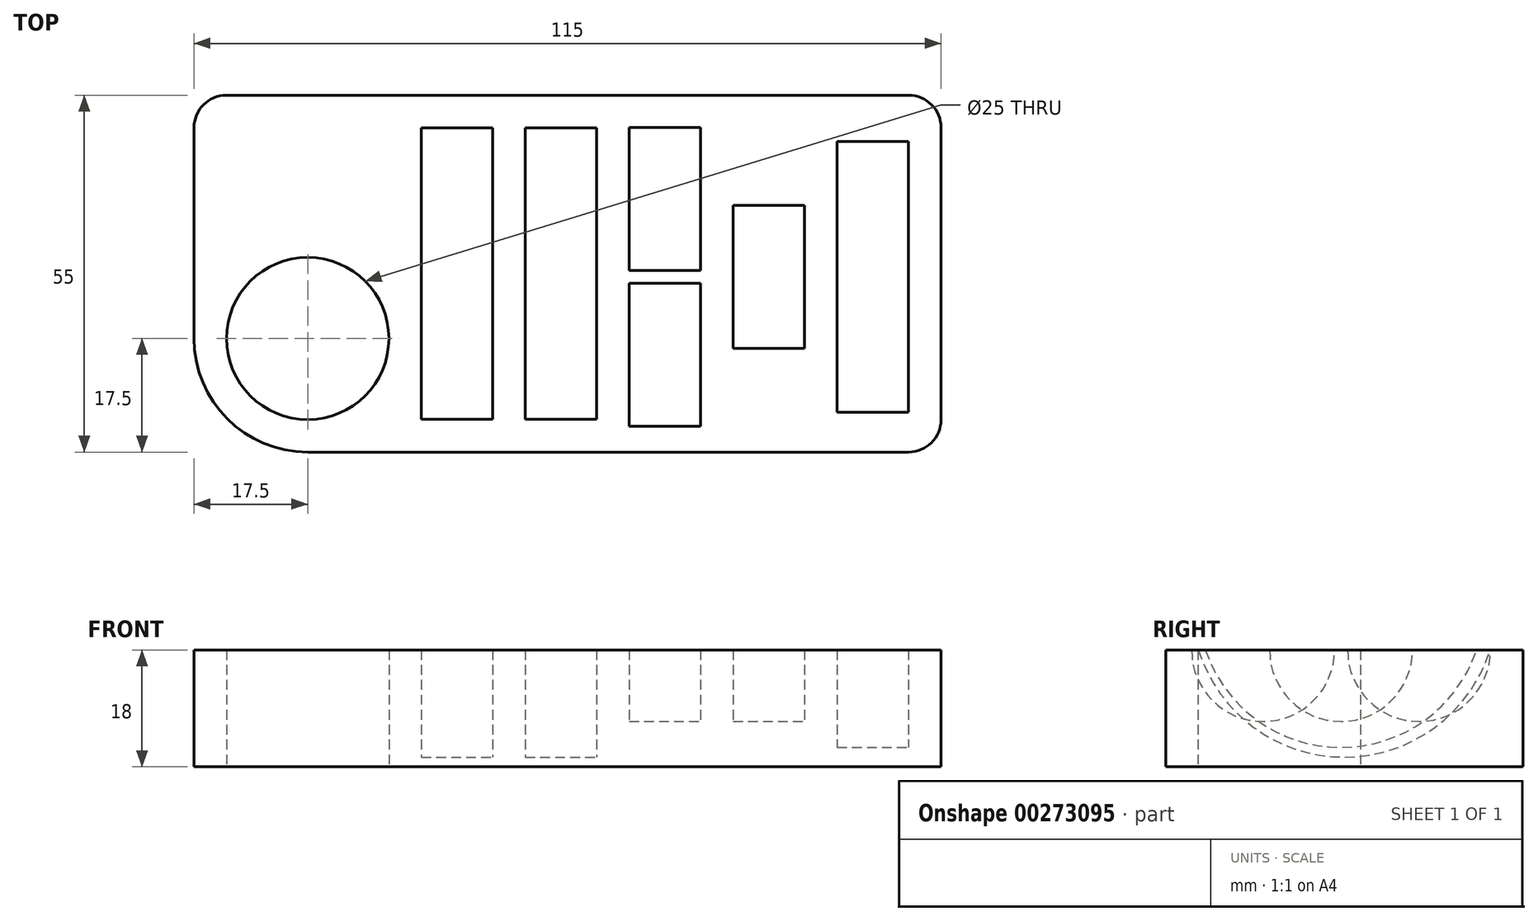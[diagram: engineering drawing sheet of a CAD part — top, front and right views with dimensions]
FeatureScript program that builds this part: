
annotation { "Feature Type Name" : "Feature", "Feature Type Description" : "" }
export const myFeature = defineFeature(function(context is Context, id is Id, definition is map)
    precondition{}
    {
        {
            var Q0;
            Q0=qCreatedBy(makeId("Top.planeOp"),FACE);
            var sketch = newSketch(context, id + "F0", { "sketchPlane" : qUnion([Q0])});
            skLineSegment(sketch, "E0.bottom", {"start": v(17.5, 0) * mm, "end": v(110, 0) * mm});
            skLineSegment(sketch, "E0.top", {"start": v(5, 55) * mm, "end": v(110, 55) * mm});
            skLineSegment(sketch, "E0.left", {"start": v(0, 17.5) * mm, "end": v(0, 50) * mm});
            skLineSegment(sketch, "E0.right", {"start": v(115, 5) * mm, "end": v(115, 50) * mm});
            skLineSegment(sketch, "E1.bottom", {"start": v(0, 0) * mm, "end": v(17.5, 0) * mm, "construction": true});
            skLineSegment(sketch, "E1.top", {"start": v(0, 17.5) * mm, "end": v(17.5, 17.5) * mm, "construction": true});
            skLineSegment(sketch, "E1.left", {"start": v(0, 0) * mm, "end": v(0, 17.5) * mm, "construction": true});
            skLineSegment(sketch, "E1.right", {"start": v(17.5, 0) * mm, "end": v(17.5, 17.5) * mm, "construction": true});
            skCircle(sketch, "E2", {"center": v(17.5, 17.5) * mm, "radius": 12.5 * mm});
            skPoint(sketch, "E3.visualSharp", {"position": v(0, 0) * mm});
            skArc(sketch, "E3.filletArc", {"start": v(0, 17.5) * mm, "mid": v(5.13, 5.13) * mm, "end": v(17.5, 0) * mm});
            skPoint(sketch, "E4.visualSharp", {"position": v(0, 55) * mm});
            skArc(sketch, "E4.filletArc", {"start": v(5, 55) * mm, "mid": v(1.46, 53.54) * mm, "end": v(0, 50) * mm});
            skPoint(sketch, "E5.visualSharp", {"position": v(115, 55) * mm});
            skArc(sketch, "E5.filletArc", {"start": v(115, 50) * mm, "mid": v(113.54, 53.54) * mm, "end": v(110, 55) * mm});
            skPoint(sketch, "E6.visualSharp", {"position": v(115, 0) * mm});
            skArc(sketch, "E6.filletArc", {"start": v(110, 0) * mm, "mid": v(113.54, 1.46) * mm, "end": v(115, 5) * mm});
            skSolve(sketch);
        }
        {
            var Q0;
            Q0=makeQuery(id+"F0.imprint","IMPRINT",FACE,{"disambiguationData":[TD([[makeQuery(id+"F0.imprint","IMPRINT",EDGE,{"derivedFrom":sQuery(id+"F0.wireOp",EDGE,"E0.bottom")}),1.0]])]});
            extrude(context, id + "F1", {"entities" : qUnion([Q0]), "depth" : 25 * mm});
        }
        {
            var Q0;
            Q0=makeQuery(id+"F1.opExtrude","CAP_FACE",FACE,{"disambiguationData":[OSD([sQuery(id+"F0.wireOp",EDGE,"E0.bottom"),sQuery(id+"F0.wireOp",EDGE,"E0.top"),sQuery(id+"F0.wireOp",EDGE,"E0.right"),sQuery(id+"F0.wireOp",EDGE,"E2"),sQuery(id+"F0.wireOp",EDGE,"E3.filletArc"),sQuery(id+"F0.wireOp",EDGE,"E4.filletArc"),sQuery(id+"F0.wireOp",EDGE,"E5.filletArc"),sQuery(id+"F0.wireOp",EDGE,"E6.filletArc")])],"isStart":false});
            var sketch = newSketch(context, id + "F2", { "sketchPlane" : qUnion([Q0])});
            skLineSegment(sketch, "E7.bottom", {"start": v(0, 0) * mm, "end": v(35, 0) * mm, "construction": true});
            skLineSegment(sketch, "E7.top", {"start": v(0, 27.5) * mm, "end": v(35, 27.5) * mm, "construction": true});
            skLineSegment(sketch, "E7.left", {"start": v(0, 0) * mm, "end": v(0, 27.5) * mm, "construction": true});
            skLineSegment(sketch, "E7.right", {"start": v(35, 0) * mm, "end": v(35, 27.5) * mm, "construction": true});
            skLineSegment(sketch, "E8.bottom", {"start": v(35, 27.5) * mm, "end": v(46, 27.5) * mm});
            skLineSegment(sketch, "E8.top", {"start": v(35, 4) * mm, "end": v(46, 4) * mm});
            skLineSegment(sketch, "E8.left", {"start": v(35, 27.5) * mm, "end": v(35, 4) * mm});
            skLineSegment(sketch, "E8.right", {"start": v(46, 27.5) * mm, "end": v(46, 4) * mm});
            skLineSegment(sketch, "E9", {"start": v(46, 27.5) * mm, "end": v(51, 27.5) * mm, "construction": true});
            skLineSegment(sketch, "E10.bottom", {"start": v(51, 27.5) * mm, "end": v(62, 27.5) * mm});
            skLineSegment(sketch, "E10.top", {"start": v(51, 4) * mm, "end": v(62, 4) * mm});
            skLineSegment(sketch, "E10.left", {"start": v(51, 27.5) * mm, "end": v(51, 4) * mm});
            skLineSegment(sketch, "E10.right", {"start": v(62, 27.5) * mm, "end": v(62, 4) * mm});
            skSolve(sketch);
        }
        {
            var Q0;
            Q0=makeQuery(id+"F2.imprint","IMPRINT",FACE,{"disambiguationData":[TD([[makeQuery(id+"F2.imprint","IMPRINT",EDGE,{"derivedFrom":sQuery(id+"F2.wireOp",EDGE,"E8.bottom")}),-1.0]])]});
            var Q1;
            Q1=makeQuery(id+"F2.imprint","IMPRINT",FACE,{"disambiguationData":[TD([[makeQuery(id+"F2.imprint","IMPRINT",EDGE,{"derivedFrom":sQuery(id+"F2.wireOp",EDGE,"E10.bottom")}),-1.0]])]});
            var Q2;
            Q2=sQuery(id+"F2.wireOp",EDGE,"E8.bottom");
            revolve(context, id + "F3", {"operationType" : NewBodyOperationType.REMOVE, "entities" : qUnion([Q0, Q1]), "axis" : qUnion([Q2]), "revolveType" : RevolveType.FULL, "oppositeDirection" : true});
        }
        {
            var Q0;
            Q0=makeQuery(id+"F1.opExtrude","SWEPT_FACE",FACE,{"disambiguationData":[OSD([sQuery(id+"F0.wireOp",EDGE,"E0.bottom")])]});
            var sketch = newSketch(context, id + "F4", { "sketchPlane" : qUnion([Q0])});
            skLineSegment(sketch, "E11", {"start": v(0, 0) * mm, "end": v(0, 18) * mm, "construction": true});
            skLineSegment(sketch, "E12.bottom", {"start": v(0, 18) * mm, "end": v(147.38, 18) * mm});
            skLineSegment(sketch, "E12.top", {"start": v(0, 40) * mm, "end": v(147.38, 40) * mm});
            skLineSegment(sketch, "E12.left", {"start": v(0, 18) * mm, "end": v(0, 40) * mm});
            skLineSegment(sketch, "E12.right", {"start": v(147.38, 18) * mm, "end": v(147.38, 40) * mm});
            skSolve(sketch);
        }
        {
            var Q0;
            Q0=qSketchRegion(id+"F4",true);
            extrude(context, id + "F5", {"entities" : qUnion([Q0]), "operationType" : NewBodyOperationType.REMOVE, "endBound" : BoundingType.THROUGH_ALL, "oppositeDirection" : true, "depth" : 25 * mm});
        }
        {
            var Q0;
            Q0=makeQuery(id+"F5.boolean.opBoolean","COPY",FACE,{"derivedFrom":makeQuery(id+"F5.opExtrude","SWEPT_FACE",FACE,{"disambiguationData":[OSD([sQuery(id+"F4.wireOp",EDGE,"E12.bottom")])]})});
            var sketch = newSketch(context, id + "F6", { "sketchPlane" : qUnion([Q0])});
            skLineSegment(sketch, "E13.bottom", {"start": v(0, 0) * mm, "end": v(67, 0) * mm, "construction": true});
            skLineSegment(sketch, "E13.top", {"start": v(0, 4) * mm, "end": v(67, 4) * mm, "construction": true});
            skLineSegment(sketch, "E13.left", {"start": v(0, 0) * mm, "end": v(0, 4) * mm, "construction": true});
            skLineSegment(sketch, "E13.right", {"start": v(67, 0) * mm, "end": v(67, 4) * mm, "construction": true});
            skLineSegment(sketch, "E14", {"start": v(67, 4) * mm, "end": v(67, 50) * mm, "construction": true});
            skLineSegment(sketch, "E15.bottom", {"start": v(67, 4) * mm, "end": v(78, 4) * mm});
            skLineSegment(sketch, "E15.top", {"start": v(67, 15) * mm, "end": v(78, 15) * mm});
            skLineSegment(sketch, "E15.left", {"start": v(67, 4) * mm, "end": v(67, 15) * mm});
            skLineSegment(sketch, "E15.right", {"start": v(78, 4) * mm, "end": v(78, 15) * mm});
            skLineSegment(sketch, "E16.bottom", {"start": v(67, 50) * mm, "end": v(78, 50) * mm});
            skLineSegment(sketch, "E16.top", {"start": v(67, 39) * mm, "end": v(78, 39) * mm});
            skLineSegment(sketch, "E16.left", {"start": v(67, 50) * mm, "end": v(67, 39) * mm});
            skLineSegment(sketch, "E16.right", {"start": v(78, 50) * mm, "end": v(78, 39) * mm});
            skLineSegment(sketch, "E17", {"start": v(67, 27) * mm, "end": v(83, 27) * mm, "construction": true});
            skLineSegment(sketch, "E18.bottom", {"start": v(83, 27) * mm, "end": v(94, 27) * mm});
            skLineSegment(sketch, "E18.top", {"start": v(83, 16) * mm, "end": v(94, 16) * mm});
            skLineSegment(sketch, "E18.left", {"start": v(83, 27) * mm, "end": v(83, 16) * mm});
            skLineSegment(sketch, "E18.right", {"start": v(94, 27) * mm, "end": v(94, 16) * mm});
            skSolve(sketch);
        }
        {
            var Q0;
            Q0=makeQuery(id+"F6.imprint","IMPRINT",FACE,{"disambiguationData":[TD([[makeQuery(id+"F6.imprint","IMPRINT",EDGE,{"derivedFrom":sQuery(id+"F6.wireOp",EDGE,"E15.bottom")}),1.0]])]});
            var Q1;
            Q1=sQuery(id+"F6.wireOp",EDGE,"E15.top");
            revolve(context, id + "F7", {"operationType" : NewBodyOperationType.REMOVE, "entities" : qUnion([Q0]), "axis" : qUnion([Q1]), "revolveType" : RevolveType.FULL, "oppositeDirection" : true});
        }
        {
            var Q0;
            Q0=makeQuery(id+"F6.imprint","IMPRINT",FACE,{"disambiguationData":[TD([[makeQuery(id+"F6.imprint","IMPRINT",EDGE,{"derivedFrom":sQuery(id+"F6.wireOp",EDGE,"E18.bottom")}),-1.0]])]});
            var Q1;
            Q1=sQuery(id+"F6.wireOp",EDGE,"E18.bottom");
            revolve(context, id + "F8", {"operationType" : NewBodyOperationType.REMOVE, "entities" : qUnion([Q0]), "axis" : qUnion([Q1]), "revolveType" : RevolveType.FULL, "oppositeDirection" : true});
        }
        {
            var Q0;
            Q0=makeQuery(id+"F6.imprint","IMPRINT",FACE,{"disambiguationData":[TD([[makeQuery(id+"F6.imprint","IMPRINT",EDGE,{"derivedFrom":sQuery(id+"F6.wireOp",EDGE,"E16.bottom")}),-1.0]])]});
            var Q1;
            Q1=sQuery(id+"F6.wireOp",EDGE,"E16.top");
            revolve(context, id + "F9", {"operationType" : NewBodyOperationType.REMOVE, "entities" : qUnion([Q0]), "axis" : qUnion([Q1]), "revolveType" : RevolveType.FULL, "oppositeDirection" : true});
        }
        {
            var Q0;
            Q0=makeQuery(id+"F5.boolean.opBoolean","COPY",FACE,{"derivedFrom":makeQuery(id+"F5.opExtrude","SWEPT_FACE",FACE,{"disambiguationData":[OSD([sQuery(id+"F4.wireOp",EDGE,"E12.bottom")])]})});
            var Q1;
            Q1=makeQuery(id+"F5.boolean.opBoolean","COPY",FACE,{"derivedFrom":makeQuery(id+"F5.opExtrude","SWEPT_FACE",FACE,{"disambiguationData":[OSD([sQuery(id+"F4.wireOp",EDGE,"E12.bottom")])]})});
            cPlane(context, id + "F10", {"entities" : qUnion([Q0, Q1]), "cplaneType" : CPlaneType.OFFSET, "offset" : 7 * mm, "width" : 150 * mm, "height" : 150 * mm});
        }
        {
            var Q0;
            Q0=qCreatedBy(id+"F10.planeOp",FACE);
            var sketch = newSketch(context, id + "F11", { "sketchPlane" : qUnion([Q0])});
            skLineSegment(sketch, "E19.bottom", {"start": v(0, 0) * mm, "end": v(99, 0) * mm, "construction": true});
            skLineSegment(sketch, "E19.top", {"start": v(0, 27) * mm, "end": v(99, 27) * mm, "construction": true});
            skLineSegment(sketch, "E19.left", {"start": v(0, 0) * mm, "end": v(0, 27) * mm, "construction": true});
            skLineSegment(sketch, "E19.right", {"start": v(99, 0) * mm, "end": v(99, 27) * mm, "construction": true});
            skLineSegment(sketch, "E20.bottom", {"start": v(99, 27) * mm, "end": v(110, 27) * mm});
            skLineSegment(sketch, "E20.top", {"start": v(99, 5) * mm, "end": v(110, 5) * mm});
            skLineSegment(sketch, "E20.left", {"start": v(99, 27) * mm, "end": v(99, 5) * mm});
            skLineSegment(sketch, "E20.right", {"start": v(110, 27) * mm, "end": v(110, 5) * mm});
            skSolve(sketch);
        }
        {
            var Q0;
            Q0=makeQuery(id+"F11.imprint","IMPRINT",FACE,{"disambiguationData":[TD([[makeQuery(id+"F11.imprint","IMPRINT",EDGE,{"derivedFrom":sQuery(id+"F11.wireOp",EDGE,"E20.bottom")}),-1.0]])]});
            var Q1;
            Q1=sQuery(id+"F11.wireOp",EDGE,"E20.bottom");
            revolve(context, id + "F12", {"operationType" : NewBodyOperationType.REMOVE, "entities" : qUnion([Q0]), "axis" : qUnion([Q1]), "revolveType" : RevolveType.FULL, "oppositeDirection" : true});
        }
    });
